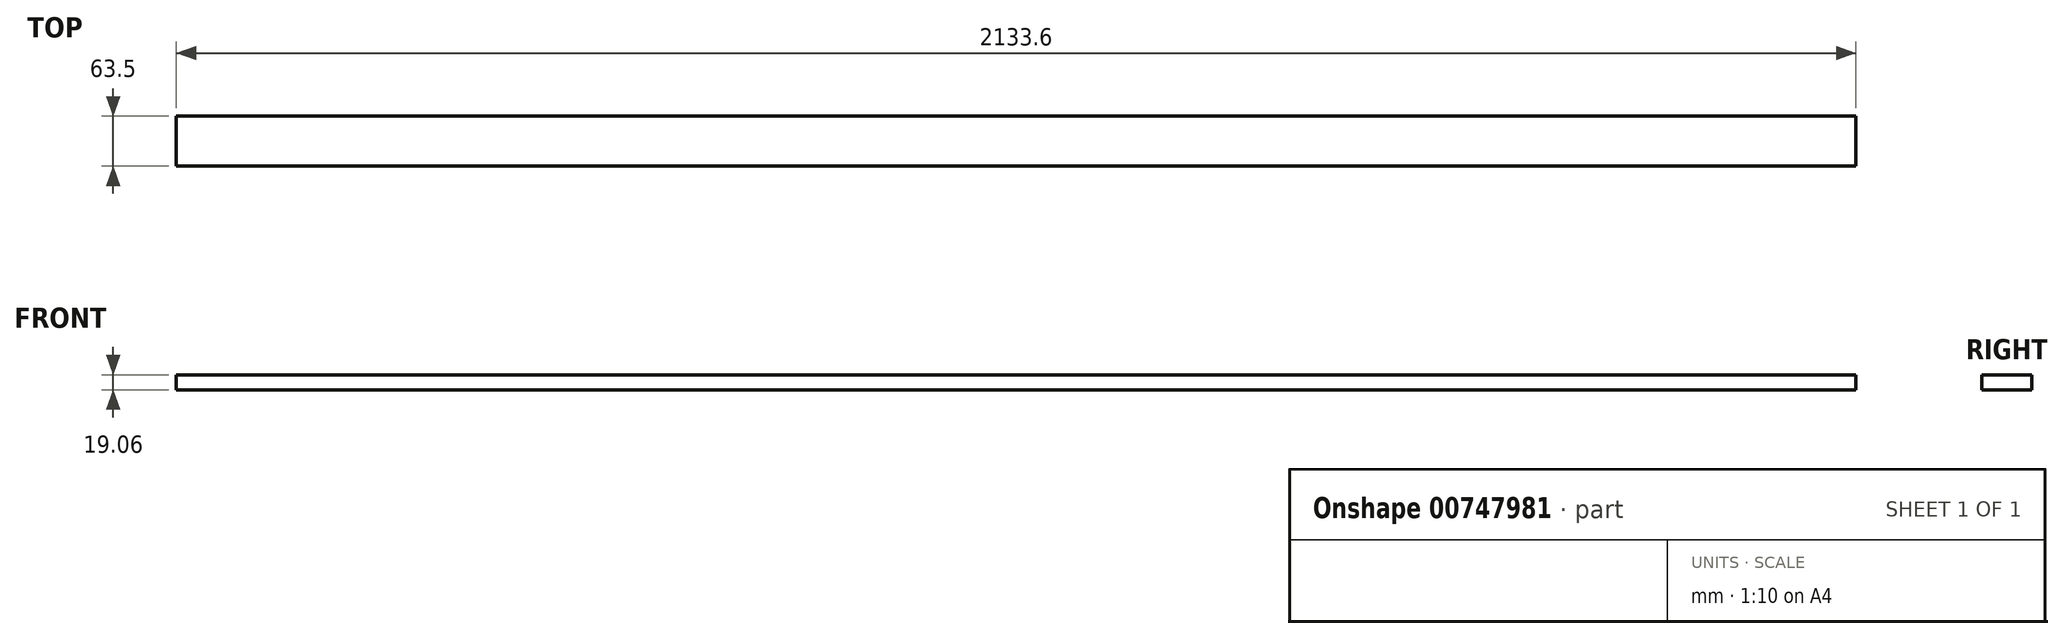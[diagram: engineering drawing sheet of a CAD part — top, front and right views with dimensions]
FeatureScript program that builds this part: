
annotation { "Feature Type Name" : "Feature", "Feature Type Description" : "" }
export const myFeature = defineFeature(function(context is Context, id is Id, definition is map)
    precondition{}
    {
        {
            var Q0;
            Q0=qCreatedBy(makeId("Front.planeOp"),FACE);
            var sketch = newSketch(context, id + "F0", { "sketchPlane" : qUnion([Q0])});
            skLineSegment(sketch, "E0.bottom", {"start": v(1066.8, 9.53) * mm, "end": v(-1066.8, 9.53) * mm});
            skLineSegment(sketch, "E0.top", {"start": v(1066.8, -9.52) * mm, "end": v(-1066.8, -9.52) * mm});
            skLineSegment(sketch, "E0.left", {"start": v(1066.8, 9.53) * mm, "end": v(1066.8, -9.52) * mm});
            skLineSegment(sketch, "E0.right", {"start": v(-1066.8, 9.53) * mm, "end": v(-1066.8, -9.52) * mm});
            skPoint(sketch, "E0.middle", {"position": v(0, 0) * mm});
            skSolve(sketch);
        }
        {
            var Q0;
            Q0 = qSketchRegion(id + "F0", true);
            extrude(context, id + "F1", {"entities" : qUnion([Q0]), "depth" : 63.5 * mm, "offsetDistance" : 25.4 * mm});
        }
    });
